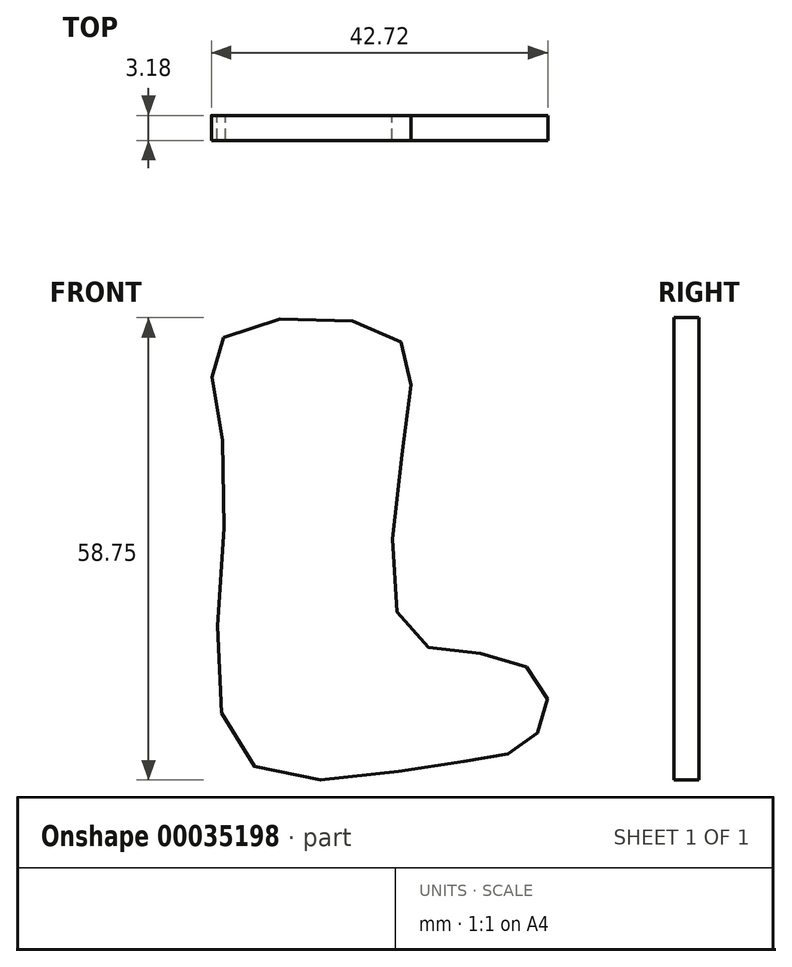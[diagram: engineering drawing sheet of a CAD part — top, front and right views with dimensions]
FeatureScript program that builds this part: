
annotation { "Feature Type Name" : "Feature", "Feature Type Description" : "" }
export const myFeature = defineFeature(function(context is Context, id is Id, definition is map)
    precondition{}
    {
        {
            var Q0;
            Q0=qCreatedBy(makeId("Front.planeOp"),FACE);
            var sketch = newSketch(context, id + "F0", { "sketchPlane" : qUnion([Q0])});
            skFitSpline(sketch, "E0", {"points": [v(-13.59, 21.9) * mm, v(7.07, 22.74) * mm, v(9.85, 12.34) * mm, v(9.85, -15.8) * mm, v(22.33, -18.72) * mm, v(27.6, -24.4) * mm, v(24.4, -30.1) * mm, v(13.87, -32.3) * mm, v(-11.23, -31.34) * mm, v(-13.45, 6.52) * mm, v(-13.59, 21.9) * mm]});
            skSolve(sketch);
        }
        {
            var Q0;
            Q0=makeQuery(id+"F0.imprint","IMPRINT",FACE,{"disambiguationData":[TD([[makeQuery(id+"F0.imprint","IMPRINT",EDGE,{"derivedFrom":sQuery(id+"F0.wireOp",EDGE,"E0")}),-1.0]])]});
            extrude(context, id + "F1", {"entities" : qUnion([Q0]), "depth" : 3.17 * mm});
        }
    });
